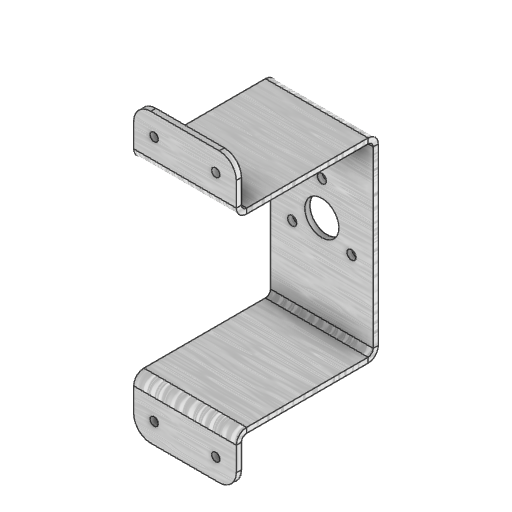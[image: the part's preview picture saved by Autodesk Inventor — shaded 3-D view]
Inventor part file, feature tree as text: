
AUTODESK INVENTOR PART (.ipt)
format: ipt  version: 2023 (Build 270158000, 158)  size: 272,384 bytes
history: native  units: mm
features: other x10, sketch x6, extrude x2, hole x1, fillet x1
ambient origin geometry x8: Origin, YZ Plane, XZ Plane, XY Plane, X Axis, Y Axis, Z Axis, Center Point
bodies: Body1 (feature_tree)
feature tree (20):
  other  "ソリッド1"
  other  "フランジ1"
  other  "フランジ2"
  extrude  "押し出し1"  Depth=30.0mm
  extrude  "押し出し3"  Depth=54.0mm
  hole  "穴1"  [1 undecoded]
  fillet  "フィレット1"  Radius=1.5mm
  sketch  "スケッチ1"
  other  "プレート1"
  sketch  "スケッチ2"
  other  "プレート2"
  other  "曲げ1"
  other  "コーナー1"
  sketch  "スケッチ3"
  other  "プレート3"
  other  "曲げ2"
  other  "コーナー2"
  sketch  "スケッチ4"
  sketch  "スケッチ6"
  sketch  "スケッチ7"
note: 1 required parameter value undecoded (feature->parameter linkage not recoverable at this tier; creation-order binding heuristic only, values carry confidence <= 0.55)
